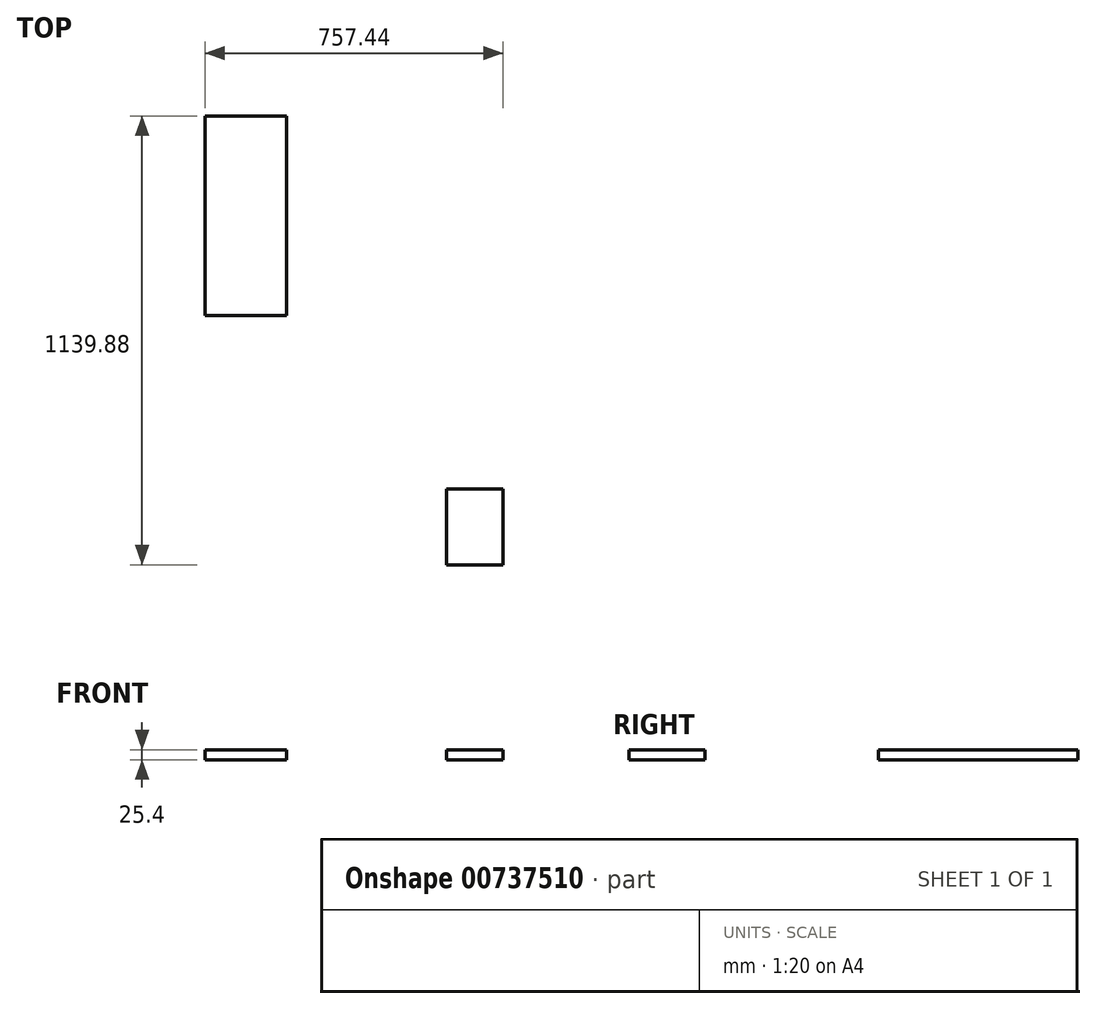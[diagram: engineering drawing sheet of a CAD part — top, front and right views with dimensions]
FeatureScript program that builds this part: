
annotation { "Feature Type Name" : "Feature", "Feature Type Description" : "" }
export const myFeature = defineFeature(function(context is Context, id is Id, definition is map)
    precondition{}
    {
        {
            var Q0;
            Q0=qCreatedBy(makeId("Top.planeOp"),FACE);
            var sketch = newSketch(context, id + "F0", { "sketchPlane" : qUnion([Q0])});
            skLineSegment(sketch, "E0.bottom", {"start": v(38.27, 187.73) * mm, "end": v(-169.7, 187.73) * mm});
            skLineSegment(sketch, "E0.top", {"start": v(38.27, -318.74) * mm, "end": v(-169.7, -318.74) * mm});
            skLineSegment(sketch, "E0.left", {"start": v(38.27, 187.73) * mm, "end": v(38.27, -318.74) * mm});
            skLineSegment(sketch, "E0.right", {"start": v(-169.7, 187.73) * mm, "end": v(-169.7, -318.74) * mm});
            skLineSegment(sketch, "E1.bottom", {"start": v(587.75, -759.25) * mm, "end": v(444.16, -759.25) * mm});
            skLineSegment(sketch, "E1.top", {"start": v(587.75, -952.15) * mm, "end": v(444.16, -952.15) * mm});
            skLineSegment(sketch, "E1.left", {"start": v(587.75, -759.25) * mm, "end": v(587.75, -952.15) * mm});
            skLineSegment(sketch, "E1.right", {"start": v(444.16, -759.25) * mm, "end": v(444.16, -952.15) * mm});
            skSolve(sketch);
        }
        {
            var Q0;
            Q0 = qSketchRegion(id + "F0", true);
            extrude(context, id + "F1", {"entities" : qUnion([Q0]), "depth" : 25.4 * mm, "offsetDistance" : 25.4 * mm});
        }
    });
